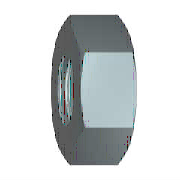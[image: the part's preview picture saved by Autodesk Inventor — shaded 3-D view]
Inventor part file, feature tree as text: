
AUTODESK INVENTOR PART (.ipt)
format: ipt  version: 2013 (Build 170138000, 138)  size: 173,568 bytes
history: native  units: mm (DEFAULTED — no unit token found)
features: sketch x3, chamfer x1, hole x1, other x1, plane x1
ambient origin geometry x7: Origin, YZ Plane, XZ Plane, X Axis, Y Axis, Z Axis, Center Point
bodies: Solid1 (feature_tree), Body (feature_tree)
feature tree (7):
  chamfer  "Chamfer1"  Distance=4.363323mm
  hole  "Thread"  [1 undecoded]
  other  "Work Axis1"
  plane  "Work Plane1"
  sketch  "Sketch1"  dims[d0=6.350853mm]
  sketch  "Sketch2"  dims[d1=2.4mm]
  sketch  "Sketch3"  dims[d2=0.0mm d3=4.363323mm d4=4.363323mm d5=5.5mm d6=5.5mm d7=90.0deg d25=2.459mm d26=6.0mm d27=4.0mm d28=2.0mm d29=14.3117mm d30=8.0mm d31=20.594885mm d8=0.270633mm d9=30.0deg d10=0.270633mm d11=30.0deg d13=0.0mm d14=0.0mm d39=0.0mm d40=0.270633mm d41=0.270633mm d42=0.0mm]
note: 1 required parameter value undecoded (feature->parameter linkage not recoverable at this tier; creation-order binding heuristic only, values carry confidence <= 0.55)
